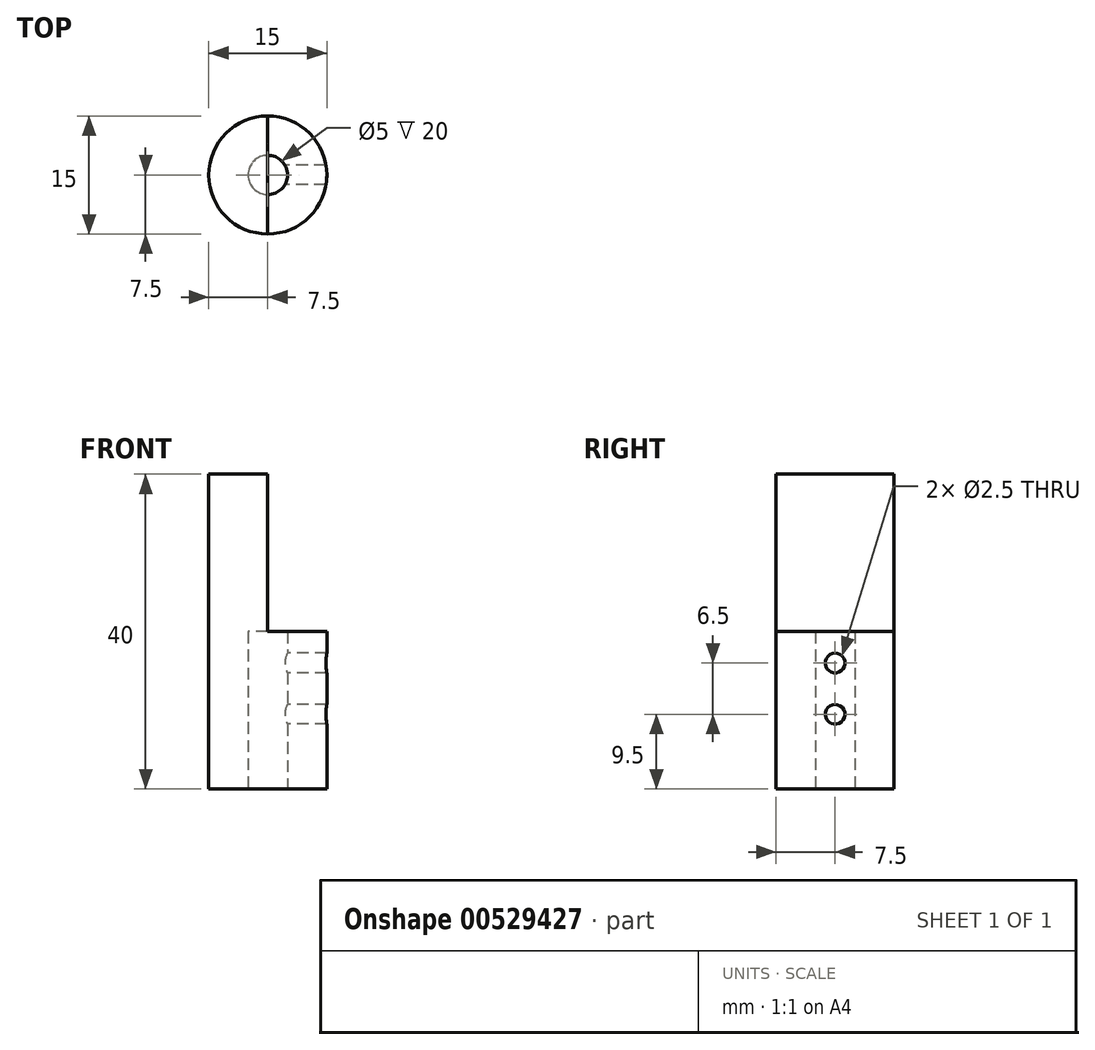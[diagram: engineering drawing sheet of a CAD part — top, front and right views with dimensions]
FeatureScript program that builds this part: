
annotation { "Feature Type Name" : "Feature", "Feature Type Description" : "" }
export const myFeature = defineFeature(function(context is Context, id is Id, definition is map)
    precondition{}
    {
        {
            var Q0;
            Q0=qCreatedBy(makeId("Top.planeOp"),FACE);
            var sketch = newSketch(context, id + "F0", { "sketchPlane" : qUnion([Q0])});
            skCircle(sketch, "E0", {"center": v(0, 0) * mm, "radius": 7.5 * mm});
            skSolve(sketch);
        }
        {
            var Q0;
            Q0 = qSketchRegion(id + "F0", true);
            extrude(context, id + "F1", {"entities" : qUnion([Q0]), "depth" : 40 * mm, "offsetDistance" : 25 * mm});
        }
        {
            var Q0;
            Q0=makeQuery(id+"F1.opExtrude","CAP_FACE",FACE,{"disambiguationData":[OSD([sQuery(id+"F0.wireOp",EDGE,"E0")])],"isStart":false});
            var sketch = newSketch(context, id + "F2", { "sketchPlane" : qUnion([Q0])});
            skLineSegment(sketch, "E1.bottom", {"start": v(0, 7.5) * mm, "end": v(31.44, 7.5) * mm});
            skLineSegment(sketch, "E1.top", {"start": v(0, -22.04) * mm, "end": v(31.44, -22.04) * mm});
            skLineSegment(sketch, "E1.left", {"start": v(0, 7.5) * mm, "end": v(0, -22.04) * mm});
            skLineSegment(sketch, "E1.right", {"start": v(31.44, 7.5) * mm, "end": v(31.44, -22.04) * mm});
            skSolve(sketch);
        }
        {
            var Q0;
            Q0 = qSketchRegion(id + "F2", true);
            extrude(context, id + "F3", {"entities" : qUnion([Q0]), "operationType" : NewBodyOperationType.REMOVE, "oppositeDirection" : true, "depth" : 20 * mm, "offsetDistance" : 25 * mm});
        }
        {
            var Q0;
            Q0=makeQuery(id+"F1.opExtrude","CAP_FACE",FACE,{"disambiguationData":[OSD([sQuery(id+"F0.wireOp",EDGE,"E0")])],"isStart":true});
            var sketch = newSketch(context, id + "F4", { "sketchPlane" : qUnion([Q0])});
            skCircle(sketch, "E2", {"center": v(0, 0) * mm, "radius": 2.5 * mm});
            skSolve(sketch);
        }
        {
            var Q0;
            Q0 = qSketchRegion(id + "F4", true);
            extrude(context, id + "F5", {"entities" : qUnion([Q0]), "operationType" : NewBodyOperationType.REMOVE, "oppositeDirection" : true, "depth" : 20 * mm, "offsetDistance" : 25 * mm});
        }
        {
            var Q0;
            Q0=makeQuery(id+"F3.boolean.opBoolean","COPY",FACE,{"derivedFrom":makeQuery(id+"F3.opExtrude","SWEPT_FACE",FACE,{"disambiguationData":[OSD([sQuery(id+"F2.wireOp",EDGE,"E1.left")])]})});
            var sketch = newSketch(context, id + "F6", { "sketchPlane" : qUnion([Q0])});
            skCircle(sketch, "E3", {"center": v(0, 16) * mm, "radius": 1.25 * mm});
            skCircle(sketch, "E4", {"center": v(0, 9.5) * mm, "radius": 1.25 * mm});
            skSolve(sketch);
        }
        {
            var Q0;
            Q0 = qSketchRegion(id + "F6", true);
            extrude(context, id + "F7", {"entities" : qUnion([Q0]), "operationType" : NewBodyOperationType.REMOVE, "depth" : 15 * mm, "offsetDistance" : 25 * mm});
        }
    });
